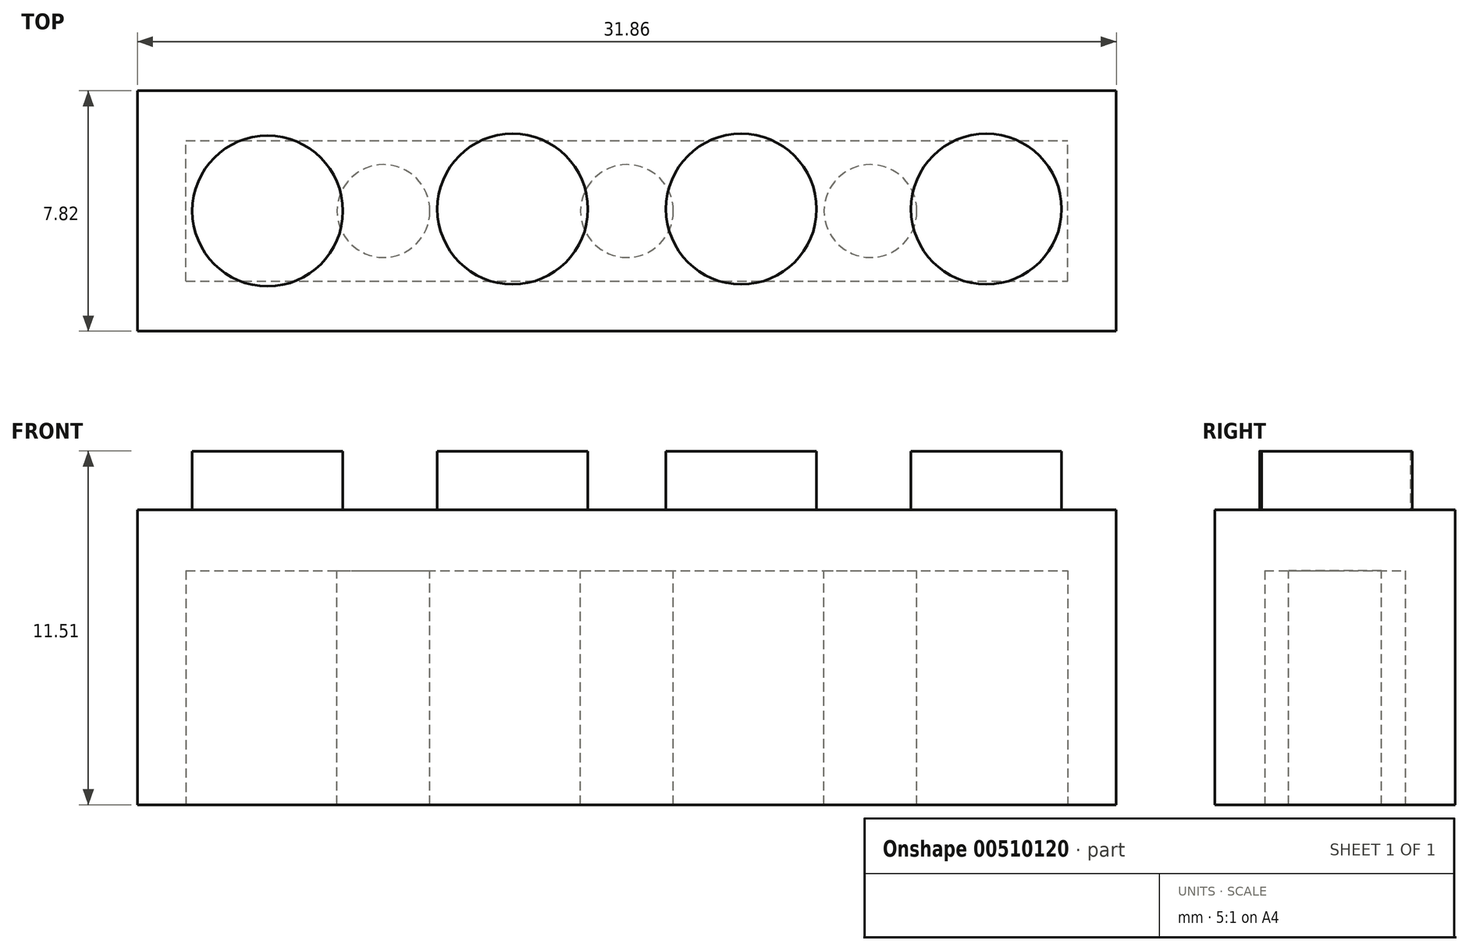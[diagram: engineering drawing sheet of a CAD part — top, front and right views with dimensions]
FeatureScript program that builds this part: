
annotation { "Feature Type Name" : "Feature", "Feature Type Description" : "" }
export const myFeature = defineFeature(function(context is Context, id is Id, definition is map)
    precondition{}
    {
        {
            var Q0;
            Q0=qCreatedBy(makeId("Top.planeOp"),FACE);
            var sketch = newSketch(context, id + "F0", { "sketchPlane" : qUnion([Q0])});
            skLineSegment(sketch, "E0.bottom", {"start": v(-15.93, 3.91) * mm, "end": v(15.93, 3.91) * mm});
            skLineSegment(sketch, "E0.top", {"start": v(-15.93, -3.91) * mm, "end": v(15.93, -3.91) * mm});
            skLineSegment(sketch, "E0.left", {"start": v(-15.93, 3.91) * mm, "end": v(-15.93, -3.91) * mm});
            skLineSegment(sketch, "E0.right", {"start": v(15.93, 3.91) * mm, "end": v(15.93, -3.91) * mm});
            skPoint(sketch, "E0.middle", {"position": v(0, 0) * mm});
            skSolve(sketch);
        }
        {
            var Q0;
            Q0=makeQuery(id+"F0.imprint","IMPRINT",FACE,{"disambiguationData":[TD([[makeQuery(id+"F0.imprint","IMPRINT",EDGE,{"derivedFrom":sQuery(id+"F0.wireOp",EDGE,"E0.bottom")}),-1.0]])]});
            extrude(context, id + "F1", {"entities" : qUnion([Q0]), "depth" : 9.6 * mm, "offsetDistance" : 25.4 * mm});
        }
        {
            var Q0;
            Q0=makeQuery(id+"F1.opExtrude","CAP_FACE",FACE,{"disambiguationData":[OSD([sQuery(id+"F0.wireOp",EDGE,"E0.bottom"),sQuery(id+"F0.wireOp",EDGE,"E0.top"),sQuery(id+"F0.wireOp",EDGE,"E0.left"),sQuery(id+"F0.wireOp",EDGE,"E0.right")])],"isStart":false});
            var sketch = newSketch(context, id + "F2", { "sketchPlane" : qUnion([Q0])});
            skCircle(sketch, "E1", {"center": v(-11.7, 0) * mm, "radius": 2.45 * mm});
            skSolve(sketch);
        }
        {
            var Q0;
            Q0 = qSketchRegion(id + "F2", true);
            extrude(context, id + "F3", {"entities" : qUnion([Q0]), "operationType" : NewBodyOperationType.ADD, "depth" : 1.9 * mm, "offsetDistance" : 25.4 * mm});
        }
        {
            var Q0;
            Q0=makeQuery(id+"F1.opExtrude","CAP_FACE",FACE,{"disambiguationData":[OSD([sQuery(id+"F0.wireOp",EDGE,"E0.bottom"),sQuery(id+"F0.wireOp",EDGE,"E0.top"),sQuery(id+"F0.wireOp",EDGE,"E0.left"),sQuery(id+"F0.wireOp",EDGE,"E0.right")])],"isStart":false});
            var sketch = newSketch(context, id + "F4", { "sketchPlane" : qUnion([Q0])});
            skCircle(sketch, "E2", {"center": v(11.7, 0.06) * mm, "radius": 2.45 * mm});
            skSolve(sketch);
        }
        {
            var Q0;
            Q0 = qSketchRegion(id + "F4", true);
            extrude(context, id + "F5", {"entities" : qUnion([Q0]), "operationType" : NewBodyOperationType.ADD, "depth" : 1.9 * mm, "offsetDistance" : 25.4 * mm});
        }
        {
            var Q0;
            Q0=makeQuery(id+"F1.opExtrude","CAP_FACE",FACE,{"disambiguationData":[OSD([sQuery(id+"F0.wireOp",EDGE,"E0.bottom"),sQuery(id+"F0.wireOp",EDGE,"E0.top"),sQuery(id+"F0.wireOp",EDGE,"E0.left"),sQuery(id+"F0.wireOp",EDGE,"E0.right")])],"isStart":false});
            var sketch = newSketch(context, id + "F6", { "sketchPlane" : qUnion([Q0])});
            skCircle(sketch, "E3", {"center": v(-3.72, 0.06) * mm, "radius": 2.45 * mm});
            skCircle(sketch, "E4", {"center": v(3.72, 0.06) * mm, "radius": 2.45 * mm});
            skSolve(sketch);
        }
        {
            var Q0;
            Q0 = qSketchRegion(id + "F6", true);
            extrude(context, id + "F7", {"entities" : qUnion([Q0]), "operationType" : NewBodyOperationType.ADD, "depth" : 1.9 * mm, "offsetDistance" : 25.4 * mm});
        }
        {
            var Q0;
            Q0=makeQuery(id+"F1.opExtrude","CAP_FACE",FACE,{"disambiguationData":[OSD([sQuery(id+"F0.wireOp",EDGE,"E0.bottom"),sQuery(id+"F0.wireOp",EDGE,"E0.top"),sQuery(id+"F0.wireOp",EDGE,"E0.left"),sQuery(id+"F0.wireOp",EDGE,"E0.right")])],"isStart":true});
            var sketch = newSketch(context, id + "F8", { "sketchPlane" : qUnion([Q0])});
            skLineSegment(sketch, "E5.bottom", {"start": v(-14.35, 2.29) * mm, "end": v(14.35, 2.29) * mm});
            skLineSegment(sketch, "E5.top", {"start": v(-14.35, -2.29) * mm, "end": v(14.35, -2.29) * mm});
            skLineSegment(sketch, "E5.left", {"start": v(-14.35, 2.29) * mm, "end": v(-14.35, -2.29) * mm});
            skLineSegment(sketch, "E5.right", {"start": v(14.35, 2.29) * mm, "end": v(14.35, -2.29) * mm});
            skPoint(sketch, "E5.middle", {"position": v(0, 0) * mm});
            skSolve(sketch);
        }
        {
            var Q0;
            Q0 = qSketchRegion(id + "F8", true);
            extrude(context, id + "F9", {"entities" : qUnion([Q0]), "operationType" : NewBodyOperationType.REMOVE, "oppositeDirection" : true, "depth" : 7.62 * mm, "offsetDistance" : 25.4 * mm});
        }
        {
            var Q0;
            Q0=makeQuery(id+"F9.boolean.opBoolean","COPY",FACE,{"derivedFrom":makeQuery(id+"F9.opExtrude","CAP_FACE",FACE,{"disambiguationData":[OSD([sQuery(id+"F8.wireOp",EDGE,"E5.bottom"),sQuery(id+"F8.wireOp",EDGE,"E5.top"),sQuery(id+"F8.wireOp",EDGE,"E5.left"),sQuery(id+"F8.wireOp",EDGE,"E5.right")])],"isStart":false})});
            var sketch = newSketch(context, id + "F10", { "sketchPlane" : qUnion([Q0])});
            skCircle(sketch, "E6", {"center": v(0, 0) * mm, "radius": 1.51 * mm});
            skCircle(sketch, "E7", {"center": v(-7.92, 0) * mm, "radius": 1.51 * mm});
            skCircle(sketch, "E8", {"center": v(7.92, 0) * mm, "radius": 1.51 * mm});
            skSolve(sketch);
        }
        {
            var Q0;
            Q0 = qSketchRegion(id + "F10", true);
            extrude(context, id + "F11", {"entities" : qUnion([Q0]), "operationType" : NewBodyOperationType.ADD, "depth" : 7.62 * mm, "offsetDistance" : 25.4 * mm});
        }
    });
